# Revit family: QF_ELECTROLUXPROFESSIONAL_1LSN26_WH6-8_E
name_source: partatom
category: Attrezzature speciali
units: mm (PartAtom-declared; Revit-internal decimal feet)

## family parameters
Basato su piano di lavoro = No
Condiviso = No
Punto di calcolo locali = No
Quota connettore circolare = Usa diametro
Sempre verticale = Sì
Taglio con vuoti quando caricato = No
Tipo di parte = Normale

## types (62) — shared parameters
Depth Actual = 721 mm  [stored 2.36549 ft]
Height Actual = 1132 mm  [stored 3.71391 ft]
Latent Heat Output = 0.0
Length Actual = 720 mm  [stored 2.3622 ft]
Modello = WH6-8
Produttore = Electrolux Professional
Sensible Heat Output = 0.0
URL = www.electroluxprofessional.com
Weight = 158
zero-valued in all types: Gas KW, Prospetto di default, Steam Pounds per Hour

## per-type parameters (varying)
| type | Cycle | Descrizione | Item Number | Phase | Volts | Watts |
| 9867630051 | 50 Hz | WASHER WH6-8 8KG EL 7,5KW 380-415/50/3N COMPASS PRO 6A01 ML 2xWATER 5xLIQ. VALV.OPEN SILVER ELS-NETW. INS. 2.I/O DISCON. | 1LSP0Z | 3 | 415 V | 3300 W |
| 9867630175 | 50 Hz | WASHER WH6-8 8KG EL 5,4KW 380-415/220-240/50/3N/3 COMPASS PRO 6G01 ML 2xWATER POWDER+5xLIQ. VALV.OPEN SILVER 2.I/O DISCO | 1L0GD1 | 3 | 415 V | 5700 W |
| 9867630202 | 50 Hz | WASHER WH6-8 8KG EL 7,5KW 380-415/50/3 COMPASS PRO 6G07 SE 2xWATER POWDER+5xLIQ. VALV.OPEN SILVER 2.I/O TRAFO DISCON. ST | 1L0GFB | 3 | 415 V | 7800 W |
| 9867630108 | 50 Hz | WASHER WH6-8 8KG EL 7,5KW 380-415/50/3N COMPASS PRO 6A01 SE 2xWATER POWDER+5xLIQ. VALV.OPEN SILVER PREP.CB INS. 2.I/O | 1LSP18 | 3 | 415 V | 3300 W |
| 9867630295 | 50 Hz | WASHER WH6-8 8KG NO HEAT 220-240/50/1N COMPASS PRO 6L01 ML 2xWATER 5xLIQ. VALV.OPEN SILVER EXT.PM. 2.I/O DISCON. | 1L0H7U | 1 | 240 V | 1000 W |
| 9867630125 | 50 Hz | WASHER WH6-8 8KG NO HEAT 220-240/50/1N COMPASS PRO 6L01 ML 2xWATER POWDER+5xLIQ. VALV.OPEN SILVER EXT.PM. 2.I/O DISCON. | 1LSP3A | 1 | 240 V | 1000 W |
| 9867630128 | 50 Hz | WASHER WH6-8 8KG NO HEAT 220-240/50/1N COMPASS PRO 6L01 ML 2xWATER POWDER+5xLIQ. VALV.OPEN SST/SILVER EXT.PM. 2.I/O DISC | 1LSP3B | 1 | 240 V | 1000 W |
| 9867630054 | 50 Hz | WASHER WH6-8 8KG MOP 7,5KW 220-240/50/3 COMPASS PRO 6M14 ML 2xWATER POWDER+5xLIQ. EL.VALV.OPEN SILVER 2.I/O QC DISCON. S | 1L0HFJ | 3 | 240 V | 7800 W |
| 9867630049 | 50 Hz | WASHER WH6-8 8KG EL 7,5KW 220-240/50/3 COMPASS PRO 6A01 ML 2xWATER POWDER+5xLIQ. VALV.OPEN SILVER 2.I/O DISCON. | 1LSP0X | 3 | 240 V | 7800 W |
| 9867630059 | 50 Hz | WASHER WH6-8 8KG LE 3KW 380-415/50/3N COMPASS PRO 6A01 SE 2xWATER POWDER+5xLIQ. VALV.OPEN SILVER PREP.CB INS. 2.I/O | 1LSP13 | 3 | 415 V | 3300 W |
| 9867630205 | 60 Hz | WASHER WH6-8 8KG EL 5,4KW 440/60/3 COMPASS PRO 6G01 ML 2xWATER POWDER+5xLIQ. PUMP SST/SILVER 2.I/O TRAFO DISCON. STOP | 1L0GHB | 3 | 440 V | 5700 W |
| 9867630192 | 60 Hz | WASHER WH6-8 8KG NO HEAT 220-240/60/1N COMPASS PRO 6L01 ML 2xWATER POWDER+5xLIQ. VALV.OPEN SILVER EXT.PM. 2.I/O DISCON. | 1L0GE9 | 1 | 240 V | 1000 W |
| 9867630152 | 50 Hz | WASHER WH6-8 8KG LE 3KW 380-400/50/3N COMPASS PRO 6A01 SE 2xWATER 5xLIQ. EL.VALV.OPEN SILVER ELS-NETW. INS. 2.I/O | 1LSP7Y | 3 | 415 V | 3300 W |
| 9867630301 | 50 Hz | WASHER WH6-8 8KG LE 3KW 220-240/50/1N COMPASS PRO 6L07 ML 2xWATER POWDER+5xLIQ. VALV.OPEN SILVER 2.I/O DISCON. | 1LM0B5 | 1 | 240 V | 3300 W |
| 98676L6000 | 50 Hz | Forecast L6000 Components | 1LSNWH | 1 | 240 V | 0 W |
| 9867630053 | 50 Hz | WASHER WH6-8 8KG MOP 7,5KW 380-400/50/3N COMPASS PRO 6M14 ML 2xWATER POWDER+5xLIQ. EL.VALV.OPEN SILVER 2.I/O QC DISCON. | 1L0G8C | 3 | 415 V | 3300 W |
| 9867630063 | 50 Hz | WASHER WH6-8 8KG LE 3KW 380-415/50/3N COMPASS PRO 6A01 SE 2xWATER POWDER VALV.OPEN SILVER INS. | 1L0FZH | 3 | 415 V | 3300 W |
| 9867630270 | 50 Hz | WASHER WH6-8 8KG EL 7,5KW 380-415/50/3N COMPASS PRO 6H12 ML 2xWATER POWDER+5xLIQ. VALV.OPEN SILVER 2.I/O QC DISCON. STOP | 1L0H18 | 3 | 415 V | 7800 W |
| 9867630117 | 50 Hz | WASHER WH6-8 8KG MOP 7,5KW 380-400/50/3N COMPASS PRO 6M14 ML 2xWATER POWDER+5xLIQ. EL.VALV.OPEN SILVER 2.I/O DISCON. STO | 1LSP39 | 3 | 415 V | 7800 W |
| 9867630288 | 60 Hz | WASHER WH6-8 8KG EL 5,4KW 220-240/60/1N COMPASS PRO 6G07 ML 2xWATER POWDER+5xLIQ. VALV.OPEN SILVER 2.I/O DISCON. STOP | 1L0H4C | 1 | 240 V | 5700 W |
| 9867630127 | 50 Hz | WASHER WH6-8 8KG EL 7,5KW 380-415/50/3N COMPASS PRO 6R01 SE 2xWATER POWDER+5xLIQ. EL.VALV.OPEN SILVER INS. 2.I/O QC DISC | 1L823H | 3 | 415 V | 3300 W |
| 9867630230 | 50 Hz | WASHER WH6-8 8KG EL 7,5KW 380-415/220-240/50/3N/3 COMPASS PRO 6L01 ML 2xWATER POWDER PUMP SILVER EXT.PM. 2.I/O DISCON. | 1LA21X | 3 | 415 V | 7800 W |
| 9867630298 | 60 Hz | WASHER WH6-8 8KG EL 7,5KW 380-415/220-240/50/3N/3 COMPASS PRO 6L01 ML 2xWATER POWDER PUMP SILVER EXT.PM. 2.I/O DISCON. | 1LT633 | 3 | 480 V | 7800 W |
| 9867630046 | 50 Hz | WASHER WH6-8 8KG EL 7,5KW 380-415/220-240/50/3N/3 COMPASS PRO 6G01 ML 2xWATER POWDER VALV.OPEN SILVER DISCON. STOP | 1L0G8A | 3 | 415 V | 5700 W |
| 9867630248 | 50 Hz | WASHER WH6-8 8KG EL 7,5KW 380-415/220-240/50/3N/1N COMPASS PRO 6G01 ML 2xWATER POWDER+5xLIQ. PUMP SILVER 2.I/O DISCON. S | 1L0GSH | 3 | 415 V | 7800 W |
| 9867630056 | 50 Hz | WASHER WH6-8 8KG LE 3KW 380-415/50/3N COMPASS PRO 6A01 SE 2xWATER POWDER VALV.OPEN SILVER ELS-NETW. INS. | 1LSP10 | 3 | 415 V | 3300 W |
| 9867630302 | 50 Hz | WASHER WH6-8 8KG LE 3KW 220-240/50/1N COMPASS PRO 6L07 ML 2xWATER POWDER+5xLIQ. PUMP SILVER 2.I/O DISCON. | 1LM0B6 | 1 | 240 V | 3300 W |
| 9867630309 | 50 Hz | WASHER WH6-8 8KG EL 7,5KW 380-415/50/3N COMPASS PRO 6H12 SE 2xWATER POWDER+5xLIQ. VALV.OPEN SILVER 2.I/O QC DISCON. STOP | 1LT65F | 3 | 415 V | 7800 W |
| 9867630238 | 50 Hz | WASHER WH6-8 8KG EL 7,5KW 380-415/50/3N COMPASS PRO 6G01 ML 2xWATER 5xLIQ. PUMP SILVER 2.I/O DISCON. STOP | 1L999X | 3 | 415 V | 3300 W |
| 9867630253 | 50 Hz | WASHER WH6-8 8KG NO HEAT 200/50/60/3 COMPASS PRO 6L41 JP,EN 2xWATER POWDER+5xLIQ. VALV.OPEN SILVER 2.I/O DISCON. | 1L0GV0 | 3 | 200 V | 1000 W |
| 9867630307 | 50 Hz | WASHER WH6-8 8KG EL 7,5KW 380-415/50/3 COMPASS PRO 6G07 ML 2xWATER POWDER+5xLIQ. VALV.OPEN SST INS. 2.I/O QC TRAFO DISCO | 1LT655 | 3 | 415 V | 7800 W |
| 9867630124 | 50 Hz | WASHER WH6-8 8KG MOP 7,5KW 380-400/50/3N COMPASS PRO 6M14 SE 2xWATER POWDER+5xLIQ. EL.VALV.OPEN SILVER INS. 2.I/O QC DIS | 1L823F | 3 | 415 V | 3300 W |
| 9867630327 | 50 Hz | WASHER WH6-8 8KG MOP 7,5KW 220-240/50/1N COMPASS PRO 6M14 ML 2xWATER POWDER+5xLIQ. EL.VALV.OPEN SILVER 2.I/O DISCON. STO | 1L0HKG | 1 | 240 V | 7800 W |
| 9867630055 | 50 Hz | WASHER WH6-8 8KG MOP 7,5KW 220-230/50/3 COMPASS PRO 6M14 ML 2xWATER POWDER+5xLIQ. EL.VALV.OPEN SILVER 2.I/O DISCON. STOP | 1L0G8D | 3 | 240 V | 7800 W |
| 9867630141 | 50 Hz | WASHER WH6-8 8KG EL 7,5KW 380-415/220-240/50/3N/1 COMPASS PRO 6H01 ML 2xWATER POWDER+5xLIQ. EL.VALV.OPEN SILVER 2.I/O DI | 1L823P | 3 | 415 V | 7800 W |
| 9867630161 | 50 Hz | WASHER WH6-8 8KG EL 5,4KW 380-415/220-240/60/3N/3 COMPASS PRO 6G01 ML 2xWATER POWDER+5xLIQ. VALV.OPEN SILVER 2.I/O DISCO | 1L0G9Y | 3 | 415 V | 5700 W |
| 9867630300 | 50 Hz | WASHER WH6-8 8KG EL 7,5KW 380-415/50/3N COMPASS PRO 6G01 ML 2xWATER POWDER+5xLIQ. PUMP SST 2.I/O DISCON. STOP | 1LM0AH | 3 | 415 V | 7800 W |
| 9867630111 | 50 Hz | WASHER WH6-8 8KG EL 7,5KW 380-415/50/3N COMPASS PRO 6G01 ML 2xWATER POWDER+5xLIQ. PUMP SILVER 2.I/O DISCON. STOP | 1LSP37 | 3 | 415 V | 3300 W |
| 9867630050 | 50 Hz | WASHER WH6-8 8KG EL 7,5KW 380-415/50/3N COMPASS PRO 6A01 ML 2xWATER POWDER VALV.OPEN SILVER ELS-NETW. DISCON. | 1LSP0Y | 3 | 415 V | 3300 W |
| 9867630060 | 50 Hz | WASHER WH6-8 8KG EL 7,5KW 380-415/50/3N COMPASS PRO 6H12 SE 2xWATER POWDER+5xLIQ. VALV.OPEN SILVER 2.I/O DISCON. STOP | 1L0G8E | 3 | 415 V | 3300 W |
| 9867630305 | 50 Hz | WASHER WH6-8 8KG LE 3KW 220-240/50/1N COMPASS PRO 6G01 ML 2xWATER POWDER+5xLIQ. PUMP SST 2.I/O DISCON. STOP | 1L82CT | 1 | 240 V | 3300 W |
| 9867630119 | 50 Hz | WASHER WH6-8 8KG EL 7,5KW 380-415/220-240/50/3N/3 COMPASS PRO 6L01 ML 2xWATER POWDER+5xLIQ. VALV.OPEN SILVER EXT.PM. 2.I | 1L823C | 3 | 415 V | 5700 W |
| 9867630109 | 50 Hz | WASHER WH6-8 8KG EL 7,5KW 380-415/50/3N COMPASS PRO 6A01 SE 2xWATER POWDER VALV.OPEN SILVER ELS-NETW. INS. | 1LSP19 | 3 | 415 V | 3300 W |
| 9867630328 | 50 Hz | WASHER WH6-8 8KG LE 3KW 220-240/50/1N COMPASS PRO 6A01 ML 2xWATER POWDER+5xLIQ. EL.VALV.OPEN SILVER 2.I/O DISCON. | 1L0HKC | 1 | 240 V | 3300 W |
| 9867630126 | 50 Hz | WASHER WH6-8 8KG NO HEAT 220-240/50/1N COMPASS PRO 6L01 ML 2xWATER POWDER+5xLIQ. VALV.OPEN SILVER EXT.PM. 2.I/O DISCON. | 1L823G | 1 | 240 V | 1000 W |
| 9867630308 | 50 Hz | WASHER WH6-8 8KG EL 7,5KW 380-415/50/3 COMPASS PRO 6G07 ML 2xWATER POWDER+5xLIQ. PUMP SST INS. 2.I/O QC TRAFO DISCON. ST | 1LT656 | 3 | 415 V | 7800 W |
| 9867630048 | 50 Hz | WASHER WH6-8 8KG EL 7,5KW 380-415/50/3N COMPASS PRO 6G01 ML 2xWATER POWDER+5xLIQ. VALV.OPEN SILVER 2.I/O DISCON. STOP | 1L0G8B | 3 | 415 V | 3300 W |
| 9867630244 | 60 Hz | WASHER WH6-8 8KG NO HEAT 208-240/60/1 COMPASS PRO 6L01 ML 2xWATER POWDER+5xLIQ. VALV.OPEN SILVER ELS-NETW. 2.I/O | 1L0GP1 | 1 | 240 V | 1000 W |
| 9867630068 | 50 Hz | WASHER WH6-8 8KG MOP 7,5KW 380-400/50/3N COMPASS PRO 6M16 ML 2xWATER POWDER+5xLIQ. EL.VALV.CLOSED SILVER 2.I/O DISCON. S | 1L822T | 3 | 415 V | 3300 W |
| 9867630047 | 50 Hz | WASHER WH6-8 8KG EL 7,5KW 380-415/50/3N COMPASS PRO 6A01 ML 2xWATER POWDER VALV.OPEN SILVER DISCON. | 1LSP0W | 3 | 415 V | 3300 W |
| 9867630204 | 60 Hz | WASHER WH6-8 8KG EL 7,5KW 440/60/3 COMPASS PRO 6G07 ML 2xWATER POWDER+5xLIQ. PUMP SST INS. 2.I/O QC TRAFO DISCON. STOP | 1L0GGD | 3 | 440 V | 5700 W |
| 9867630057 | 50 Hz | WASHER WH6-8 8KG LE 3KW 380-400/50/3N COMPASS PRO 6A01 SE 2xWATER 5xLIQ. VALV.OPEN SILVER ELS-NETW. INS. 2.I/O | 1LSP11 | 3 | 415 V | 3300 W |
| 9867630058 | 50 Hz | WASHER WH6-8 8KG LE 3KW 380-415/50/3N COMPASS PRO 6A01 SE 2xWATER 5xLIQ. VALV.OPEN SILVER INS. 2.I/O | 1LSP12 | 3 | 415 V | 3300 W |
| 9867630037 | 50 Hz | WASHER WH6-8 8KG EL 7,5KW 380-415/50/3N COMPASS PRO 6G01 ML 2xWATER POWDER VALV.OPEN SILVER DISCON. STOP | 1L0G87 | 3 | 415 V | 7800 W |
| 9867630163 | 50 Hz | WASHER WH6-8 8KG MOP 7,5KW 380-415/220-240/50/3N/3 COMPASS PRO 6M14 ML 2xWATER POWDER+5xLIQ. EL.VALV.OPEN SILVER 2.I/O Q | 1L0GA0 | 3 | 415 V | 5700 W |
| 9867630306 | 50 Hz | WASHER WH6-8 8KG LE 3KW 220-240/50/1 COMPASS PRO 6G07 ML 2xWATER POWDER+5xLIQ. VALV.OPEN SST/SILVER 2.I/O QC DISCON. STO | 1L82D3 | 1 | 240 V | 3300 W |
| 9867630113 | 50 Hz | WASHER WH6-8 8KG EL 7,5KW 380-415/50/3N COMPASS PRO 6A01 ML 2xWATER POWDER+5xLIQ. VALV.OPEN SILVER EXT.PM. INS. 2.I/O DI | 1LSP1B | 3 | 415 V | 3300 W |
| 9867630267 | 50 Hz | WASHER WH6-8 8KG NO HEAT 220-240/50/1N COMPASS PRO 6L01 ML 2xWATER 5xLIQ. VALV.OPEN SILVER EXT.PM. 2.I/O DISCON. | 1LSPLX | 1 | 240 V | 1000 W |
| 9867630062 | 50 Hz | WASHER WH6-8 8KG EL 7,5KW 380-415/50/3N COMPASS PRO 6A01 SE 2xWATER POWDER VALV.OPEN SILVER INS. | 1LSP15 | 3 | 415 V | 3300 W |
| 9867630190 | 60 Hz | WASHER WH6-8 8KG EL 7,5KW 440/60/3 COMPASS PRO 6G07 ML 2xWATER POWDER+5xLIQ. VALV.OPEN SILVER 2.I/O QC TRAFO DISCON. STO | 1LSPBP | 3 | 440 V | 5700 W |
| 9867630170 | 50 Hz | WASHER WH6-8 8KG EL 5,4KW 380-415/220-240/50/3N/3 COMPASS PRO 6H12 ML 2xWATER POWDER+5xLIQ. VALV.OPEN SILVER 2.I/O QC DI | 1L0GBG | 3 | 415 V | 5700 W |
| 9867630110 | 50 Hz | WASHER WH6-8 8KG EL 7,5KW 380-400/50/3N COMPASS PRO 6A01 SE 2xWATER 5xLIQ. VALV.OPEN SILVER INS. 2.I/O | 1LSP1A | 3 | 415 V | 3300 W |

note: [stored X ft] marks values corroborated as IEEE doubles in the binary element streams (Revit-internal decimal feet)

## geometry (parser evidence)
native form markers: Blend x8
no freeform markers — native parametric forms only
